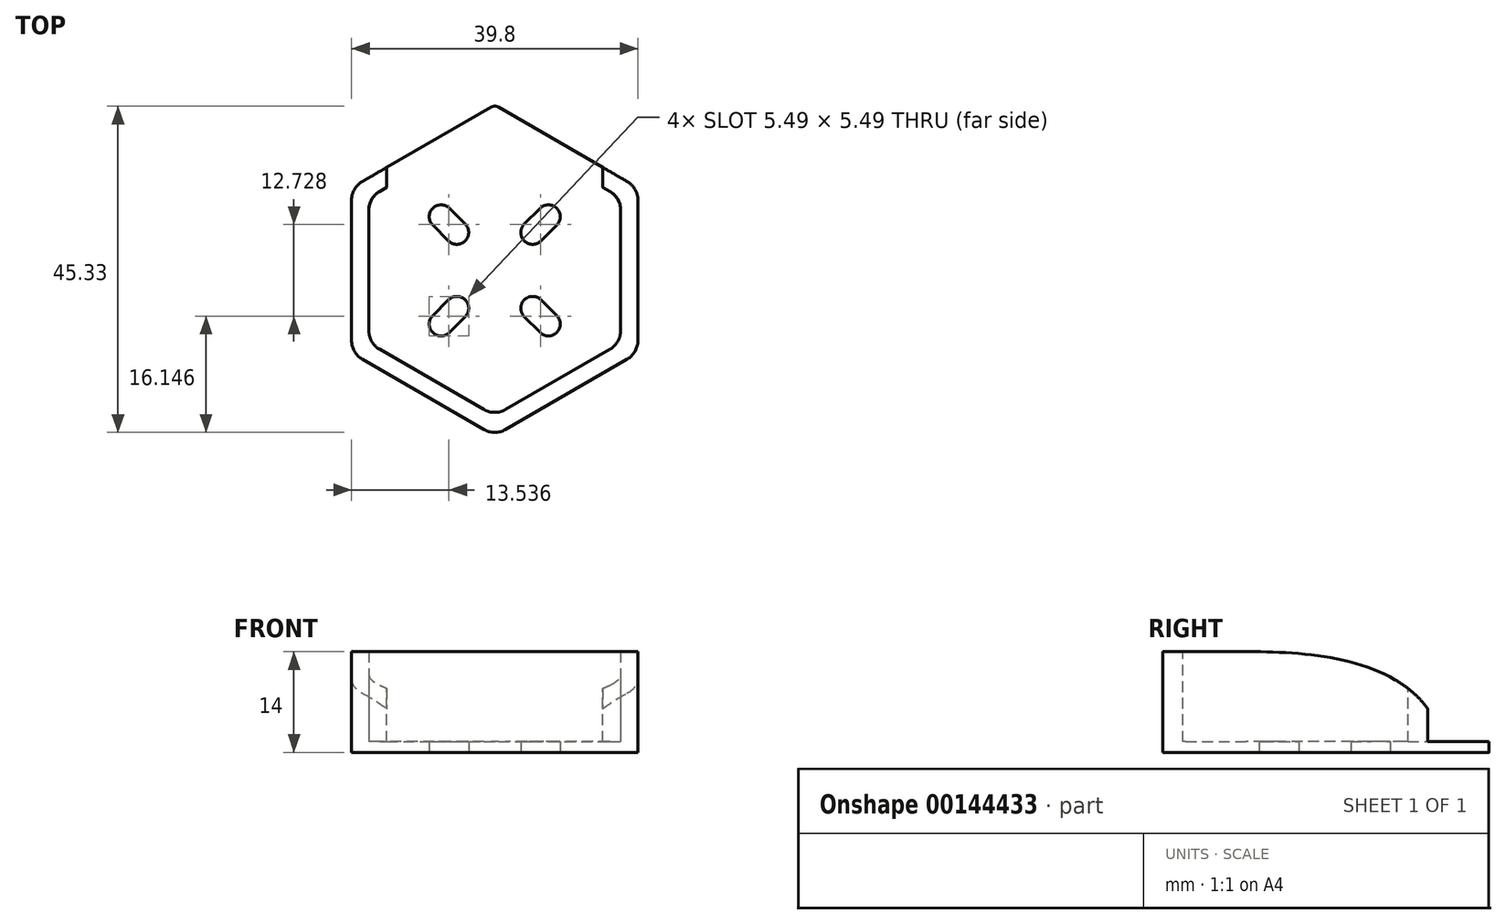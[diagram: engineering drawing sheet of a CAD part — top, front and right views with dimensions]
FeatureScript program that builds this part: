
annotation { "Feature Type Name" : "Feature", "Feature Type Description" : "" }
export const myFeature = defineFeature(function(context is Context, id is Id, definition is map)
    precondition{}
    {
        {
            var Q0;
            Q0=qCreatedBy(makeId("Top.planeOp"),FACE);
            var sketch = newSketch(context, id + "F0", { "sketchPlane" : qUnion([Q0])});
            skPoint(sketch, "E0", {"position": v(0, 0) * mm});
            skLineSegment(sketch, "E1", {"start": v(-20.56, -20.56) * mm, "end": v(20.56, 20.56) * mm, "construction": true});
            skLineSegment(sketch, "E2", {"start": v(-19.47, 19.47) * mm, "end": v(19.47, -19.47) * mm, "construction": true});
            skArc(sketch, "E3", {"start": v(-6.3, 8.63) * mm, "mid": v(-8.63, 8.63) * mm, "end": v(-8.63, 6.3) * mm});
            skArc(sketch, "E4", {"start": v(-6.43, 4.1) * mm, "mid": v(-4.1, 4.1) * mm, "end": v(-4.1, 6.43) * mm});
            skLineSegment(sketch, "E5", {"start": v(-6.3, 8.63) * mm, "end": v(-4.1, 6.43) * mm});
            skLineSegment(sketch, "E6", {"start": v(-8.63, 6.3) * mm, "end": v(-6.43, 4.1) * mm});
            skLineSegment(sketch, "E7.MirrorCS", {"start": v(-8.63, -6.3) * mm, "end": v(-6.43, -4.1) * mm});
            skArc(sketch, "E8.MirrorCS", {"start": v(-6.3, -8.63) * mm, "mid": v(-8.63, -8.63) * mm, "end": v(-8.63, -6.3) * mm});
            skArc(sketch, "E9.MirrorCS", {"start": v(-6.43, -4.1) * mm, "mid": v(-4.1, -4.1) * mm, "end": v(-4.1, -6.43) * mm});
            skLineSegment(sketch, "E10.MirrorCS", {"start": v(-6.3, -8.63) * mm, "end": v(-4.1, -6.43) * mm});
            skLineSegment(sketch, "E11.MirrorCS", {"start": v(6.3, -8.63) * mm, "end": v(4.1, -6.43) * mm});
            skLineSegment(sketch, "E12.MirrorCS", {"start": v(8.63, -6.3) * mm, "end": v(6.43, -4.1) * mm});
            skLineSegment(sketch, "E13.MirrorCS", {"start": v(6.3, 8.63) * mm, "end": v(4.1, 6.43) * mm});
            skArc(sketch, "E14.MirrorCS", {"start": v(6.43, -4.1) * mm, "mid": v(4.1, -4.1) * mm, "end": v(4.1, -6.43) * mm});
            skLineSegment(sketch, "E15.MirrorCS", {"start": v(8.63, 6.3) * mm, "end": v(6.43, 4.1) * mm});
            skArc(sketch, "E16.MirrorCS", {"start": v(6.3, -8.63) * mm, "mid": v(8.63, -8.63) * mm, "end": v(8.63, -6.3) * mm});
            skArc(sketch, "E17.MirrorCS", {"start": v(6.3, 8.63) * mm, "mid": v(8.63, 8.63) * mm, "end": v(8.63, 6.3) * mm});
            skArc(sketch, "E18.MirrorCS", {"start": v(6.43, 4.1) * mm, "mid": v(4.1, 4.1) * mm, "end": v(4.1, 6.43) * mm});
            skCircle(sketch, "E19.cCircle", {"center": v(0, 0) * mm, "radius": 17.5 * mm, "construction": true});
            skLineSegment(sketch, "E19.0", {"start": v(17.5, -10.1) * mm, "end": v(0, -20.2) * mm});
            skLineSegment(sketch, "E19.1", {"start": v(0, -20.2) * mm, "end": v(-17.5, -10.1) * mm});
            skLineSegment(sketch, "E19.2", {"start": v(-17.5, -10.1) * mm, "end": v(-17.5, 10.1) * mm});
            skLineSegment(sketch, "E19.3", {"start": v(-17.5, 10.1) * mm, "end": v(0, 20.2) * mm});
            skLineSegment(sketch, "E19.4", {"start": v(0, 20.2) * mm, "end": v(17.5, 10.1) * mm});
            skLineSegment(sketch, "E19.5", {"start": v(17.5, 10.1) * mm, "end": v(17.5, -10.1) * mm});
            skPoint(sketch, "E19.0.midPoint", {"position": v(8.75, -15.16) * mm});
            skLineSegment(sketch, "E20.0", {"start": v(-19.9, -11.49) * mm, "end": v(-19.9, 11.49) * mm});
            skLineSegment(sketch, "E20.1", {"start": v(0, 22.98) * mm, "end": v(19.9, 11.49) * mm});
            skLineSegment(sketch, "E20.2", {"start": v(19.9, 11.49) * mm, "end": v(19.9, -11.49) * mm});
            skLineSegment(sketch, "E20.3", {"start": v(-19.9, 11.49) * mm, "end": v(0, 22.98) * mm});
            skLineSegment(sketch, "E20.4", {"start": v(19.9, -11.49) * mm, "end": v(0, -22.98) * mm});
            skLineSegment(sketch, "E20.5", {"start": v(0, -22.98) * mm, "end": v(-19.9, -11.49) * mm});
            skSolve(sketch);
        }
        {
            var Q0;
            Q0=makeQuery(id+"F0.imprint","IMPRINT",FACE,{"disambiguationData":[TD([[makeQuery(id+"F0.imprint","IMPRINT",EDGE,{"derivedFrom":sQuery(id+"F0.wireOp",EDGE,"E3")}),-1.0]])]});
            extrude(context, id + "F1", {"entities" : qUnion([Q0]), "depth" : 1.5 * mm});
        }
        {
            var Q0;
            Q0=makeQuery(id+"F0.imprint","IMPRINT",FACE,{"disambiguationData":[TD([[makeQuery(id+"F0.imprint","IMPRINT",EDGE,{"derivedFrom":sQuery(id+"F0.wireOp",EDGE,"E19.0")}),1.0]])]});
            extrude(context, id + "F2", {"entities" : qUnion([Q0]), "operationType" : NewBodyOperationType.ADD, "depth" : 14 * mm, "offsetDistance" : 25 * mm});
        }
        {
            var Q0;
            Q0=qCreatedBy(makeId("Front.planeOp"),FACE);
            cPlane(context, id + "F3", {"entities" : qUnion([Q0]), "cplaneType" : CPlaneType.OFFSET, "offset" : 25 * mm, "oppositeDirection" : true, "width" : 150 * mm, "height" : 150 * mm});
        }
        {
            var Q0;
            Q0=qCreatedBy(id+"F3.planeOp",FACE);
            var sketch = newSketch(context, id + "F4", { "sketchPlane" : qUnion([Q0])});
            skLineSegment(sketch, "E21.bottom", {"start": v(-15, 1.5) * mm, "end": v(15, 1.5) * mm});
            skLineSegment(sketch, "E21.top", {"start": v(-15, 19.2) * mm, "end": v(15, 19.2) * mm});
            skLineSegment(sketch, "E21.left", {"start": v(-15, 1.5) * mm, "end": v(-15, 19.2) * mm});
            skLineSegment(sketch, "E21.right", {"start": v(15, 1.5) * mm, "end": v(15, 19.2) * mm});
            skPoint(sketch, "E21.middle", {"position": v(0, 10.35) * mm});
            skSolve(sketch);
        }
        {
            var Q0;
            Q0=makeQuery(id+"F4.imprint","IMPRINT",FACE,{"disambiguationData":[TD([[makeQuery(id+"F4.imprint","IMPRINT",EDGE,{"derivedFrom":sQuery(id+"F4.wireOp",EDGE,"E21.bottom")}),1.0]])]});
            extrude(context, id + "F5", {"entities" : qUnion([Q0]), "operationType" : NewBodyOperationType.REMOVE, "depth" : 26 * mm});
        }
        {
            var Q0;
            Q0=makeQuery(id+"F2.opExtrude","SWEPT_EDGE",EDGE,{"disambiguationData":[OSD([sQuery(id+"F0.wireOp",EDGE,"E20.1"),sQuery(id+"F0.wireOp",EDGE,"E20.2")])]});
            var Q1;
            Q1=makeQuery(id+"F2.opExtrude","SWEPT_EDGE",EDGE,{"disambiguationData":[OSD([sQuery(id+"F0.wireOp",EDGE,"E20.0"),sQuery(id+"F0.wireOp",EDGE,"E20.3")])]});
            var Q2;
            Q2=makeQuery(id+"F2.opExtrude","SWEPT_EDGE",EDGE,{"disambiguationData":[OSD([sQuery(id+"F0.wireOp",EDGE,"E20.0"),sQuery(id+"F0.wireOp",EDGE,"E20.5")])]});
            var Q3;
            Q3=makeQuery(id+"F2.opExtrude","SWEPT_EDGE",EDGE,{"disambiguationData":[OSD([sQuery(id+"F0.wireOp",EDGE,"E20.4"),sQuery(id+"F0.wireOp",EDGE,"E20.5")])]});
            var Q4;
            Q4=makeQuery(id+"F2.opExtrude","SWEPT_EDGE",EDGE,{"disambiguationData":[OSD([sQuery(id+"F0.wireOp",EDGE,"E20.2"),sQuery(id+"F0.wireOp",EDGE,"E20.4")])]});
            var Q5;
            Q5=makeQuery(id+"F2.opExtrude","SWEPT_EDGE",EDGE,{"disambiguationData":[OSD([sQuery(id+"F0.wireOp",EDGE,"E19.4"),sQuery(id+"F0.wireOp",EDGE,"E19.5")])]});
            var Q6;
            Q6=makeQuery(id+"F2.opExtrude","SWEPT_EDGE",EDGE,{"disambiguationData":[OSD([sQuery(id+"F0.wireOp",EDGE,"E19.0"),sQuery(id+"F0.wireOp",EDGE,"E19.5")])]});
            var Q7;
            Q7=makeQuery(id+"F2.opExtrude","SWEPT_EDGE",EDGE,{"disambiguationData":[OSD([sQuery(id+"F0.wireOp",EDGE,"E19.0"),sQuery(id+"F0.wireOp",EDGE,"E19.1")])]});
            var Q8;
            Q8=makeQuery(id+"F2.opExtrude","SWEPT_EDGE",EDGE,{"disambiguationData":[OSD([sQuery(id+"F0.wireOp",EDGE,"E19.1"),sQuery(id+"F0.wireOp",EDGE,"E19.2")])]});
            var Q9;
            Q9=makeQuery(id+"F2.opExtrude","SWEPT_EDGE",EDGE,{"disambiguationData":[OSD([sQuery(id+"F0.wireOp",EDGE,"E19.2"),sQuery(id+"F0.wireOp",EDGE,"E19.3")])]});
            fillet(context, id + "F6", {"entities" : qUnion([Q0, Q1, Q2, Q3, Q4, Q5, Q6, Q7, Q8, Q9]), "radius" : 3 * mm, "tangentPropagation" : true, "allowEdgeOverflow" : false});
        }
        {
            var Q0;
            Q0=makeQuery(id+"F1.opExtrude","CAP_EDGE",EDGE,{"disambiguationData":[OSD([sQuery(id+"F0.wireOp",EDGE,"E19.3")])],"isStart":false});
            var Q1;
            Q1=makeQuery(id+"F2.opExtrude","SWEPT_EDGE",EDGE,{"disambiguationData":[OSD([sQuery(id+"F0.wireOp",EDGE,"E20.1"),sQuery(id+"F0.wireOp",EDGE,"E20.3")])]});
            fillet(context, id + "F7", {"entities" : qUnion([Q0, Q1]), "radius" : 1 * mm, "tangentPropagation" : true, "allowEdgeOverflow" : false});
        }
        {
            var Q0;
            Q0=qCreatedBy(makeId("Right.planeOp"),FACE);
            var sketch = newSketch(context, id + "F8", { "sketchPlane" : qUnion([Q0])});
            skPoint(sketch, "E22.0", {"position": v(-9.76, 14) * mm});
            skFitSpline(sketch, "E23", {"points": [v(-9.76, 14) * mm, v(14.68, 5.5) * mm], "startDerivative": vector(26.14, 0) * mm, "endDerivative": vector(13.75, -21.62) * mm});
            skLineSegment(sketch, "E24", {"start": v(-9.76, 14) * mm, "end": v(14.68, 14) * mm});
            skLineSegment(sketch, "E25", {"start": v(14.68, 14) * mm, "end": v(14.68, 5.5) * mm});
            skLineSegment(sketch, "E26.0", {"start": v(22.69, 1.5) * mm, "end": v(14.32, 1.5) * mm});
            skSolve(sketch);
        }
        {
            var Q0;
            Q0 = qSketchRegion(id + "F8", true);
            extrude(context, id + "F9", {"entities" : qUnion([Q0]), "operationType" : NewBodyOperationType.REMOVE, "endBound" : BoundingType.SYMMETRIC, "depth" : 43.6 * mm, "offsetDistance" : 25 * mm});
        }
    });
